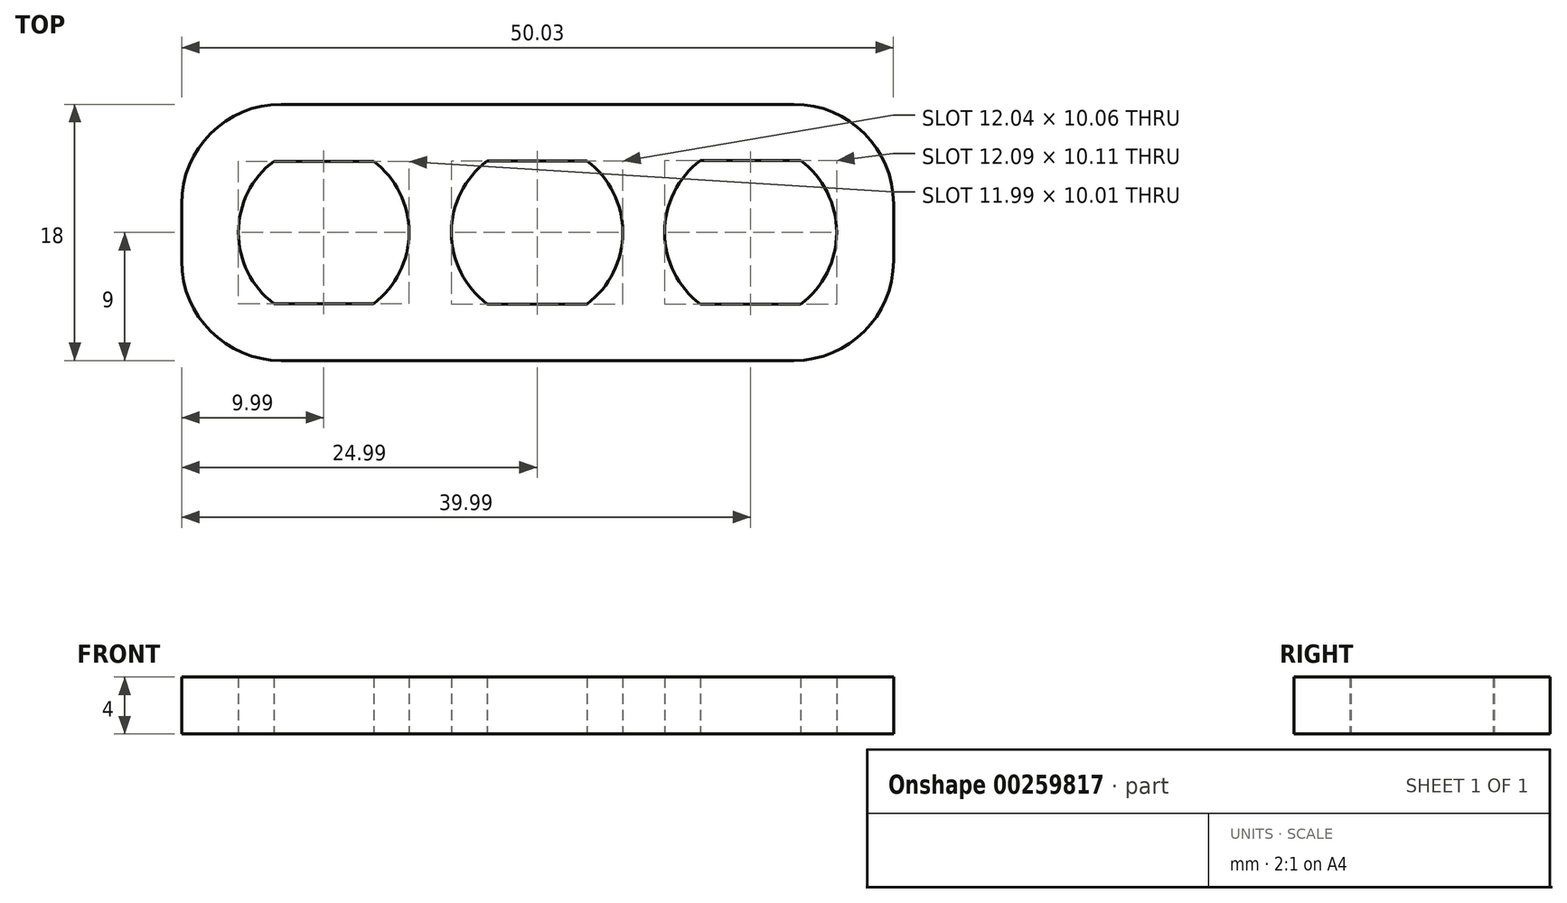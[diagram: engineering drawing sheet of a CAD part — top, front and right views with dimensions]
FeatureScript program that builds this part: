
annotation { "Feature Type Name" : "Feature", "Feature Type Description" : "" }
export const myFeature = defineFeature(function(context is Context, id is Id, definition is map)
    precondition{}
    {
        {
            var Q0;
            Q0=qCreatedBy(makeId("Top.planeOp"),FACE);
            var sketch = newSketch(context, id + "F0", { "sketchPlane" : qUnion([Q0])});
            skArc(sketch, "E0", {"start": v(-3.5, 5) * mm, "mid": v(-6, 0) * mm, "end": v(-3.5, -5) * mm, "construction": true});
            skArc(sketch, "E1", {"start": v(3.5, -5) * mm, "mid": v(6, 0) * mm, "end": v(3.5, 5) * mm, "construction": true});
            skLineSegment(sketch, "E2", {"start": v(-3.5, 5) * mm, "end": v(3.5, 5) * mm, "construction": true});
            skLineSegment(sketch, "E3", {"start": v(3.5, -5) * mm, "end": v(-3.5, -5) * mm, "construction": true});
            skPoint(sketch, "E4", {"position": v(0, 5) * mm});
            skPoint(sketch, "E5", {"position": v(-6, 0) * mm});
            skPoint(sketch, "E6", {"position": v(6, 0) * mm});
            skSolve(sketch);
        }
        {
            var Q0;
            Q0=qCreatedBy(makeId("Top.planeOp"),FACE);
            var sketch = newSketch(context, id + "F1", { "sketchPlane" : qUnion([Q0])});
            skLineSegment(sketch, "E7.0", {"start": v(-3.5, 5) * mm, "end": v(3.5, 5) * mm});
            skArc(sketch, "E8.0", {"start": v(-3.5, 5) * mm, "mid": v(-6, 0) * mm, "end": v(-3.5, -5) * mm});
            skLineSegment(sketch, "E9.0", {"start": v(3.5, -5) * mm, "end": v(-3.5, -5) * mm});
            skArc(sketch, "E10.0", {"start": v(3.5, -5) * mm, "mid": v(6, 0) * mm, "end": v(3.5, 5) * mm});
            skArc(sketch, "E11.1.0.0", {"start": v(11.5, 5) * mm, "mid": v(9, 0) * mm, "end": v(11.5, -5) * mm, "construction": true});
            skLineSegment(sketch, "E11.1.0.1", {"start": v(11.5, 5) * mm, "end": v(18.5, 5) * mm, "construction": true});
            skLineSegment(sketch, "E11.1.0.2", {"start": v(18.5, -5) * mm, "end": v(11.5, -5) * mm, "construction": true});
            skArc(sketch, "E11.1.0.3", {"start": v(18.5, -5) * mm, "mid": v(21, 0) * mm, "end": v(18.5, 5) * mm, "construction": true});
            skArc(sketch, "E11.2.0.0", {"start": v(26.5, 5) * mm, "mid": v(24, 0) * mm, "end": v(26.5, -5) * mm, "construction": true});
            skLineSegment(sketch, "E11.2.0.1", {"start": v(26.5, 5) * mm, "end": v(33.5, 5) * mm, "construction": true});
            skLineSegment(sketch, "E11.2.0.2", {"start": v(33.5, -5) * mm, "end": v(26.5, -5) * mm, "construction": true});
            skArc(sketch, "E11.2.0.3", {"start": v(33.5, -5) * mm, "mid": v(36, 0) * mm, "end": v(33.5, 5) * mm, "construction": true});
            skLineSegment(sketch, "E11.direction1", {"start": v(-3.5, -5) * mm, "end": v(11.5, -5) * mm, "construction": true});
            skArc(sketch, "E12.0", {"start": v(11.49, 5.03) * mm, "mid": v(8.98, 0) * mm, "end": v(11.49, -5.03) * mm});
            skLineSegment(sketch, "E12.1", {"start": v(11.49, 5.03) * mm, "end": v(18.51, 5.03) * mm});
            skArc(sketch, "E12.2", {"start": v(18.51, -5.03) * mm, "mid": v(21.02, 0) * mm, "end": v(18.51, 5.03) * mm});
            skLineSegment(sketch, "E12.3", {"start": v(18.51, -5.03) * mm, "end": v(11.49, -5.03) * mm});
            skArc(sketch, "E13.0", {"start": v(26.48, 5.05) * mm, "mid": v(23.96, 0) * mm, "end": v(26.48, -5.05) * mm});
            skLineSegment(sketch, "E13.1", {"start": v(26.48, 5.05) * mm, "end": v(33.52, 5.05) * mm});
            skArc(sketch, "E13.2", {"start": v(33.52, -5.05) * mm, "mid": v(36.04, 0) * mm, "end": v(33.52, 5.05) * mm});
            skLineSegment(sketch, "E13.3", {"start": v(33.52, -5.05) * mm, "end": v(26.48, -5.05) * mm});
            skLineSegment(sketch, "E14.bottom", {"start": v(-3, 9) * mm, "end": v(33.04, 9) * mm});
            skLineSegment(sketch, "E14.top", {"start": v(-3, -9) * mm, "end": v(33.04, -9) * mm});
            skLineSegment(sketch, "E14.left", {"start": v(-10, 2) * mm, "end": v(-10, -2) * mm});
            skLineSegment(sketch, "E14.right", {"start": v(40.04, 2) * mm, "end": v(40.04, -2) * mm});
            skPoint(sketch, "E15.visualSharp", {"position": v(-10, 9) * mm});
            skArc(sketch, "E15.filletArc", {"start": v(-3, 9) * mm, "mid": v(-7.94, 6.95) * mm, "end": v(-10, 2) * mm});
            skPoint(sketch, "E16.visualSharp", {"position": v(-10, -9) * mm});
            skArc(sketch, "E16.filletArc", {"start": v(-10, -2) * mm, "mid": v(-7.94, -6.95) * mm, "end": v(-3, -9) * mm});
            skPoint(sketch, "E17.visualSharp", {"position": v(40.04, -9) * mm});
            skArc(sketch, "E17.filletArc", {"start": v(33.04, -9) * mm, "mid": v(38, -6.95) * mm, "end": v(40.04, -2) * mm});
            skPoint(sketch, "E18.visualSharp", {"position": v(40.04, 9) * mm});
            skArc(sketch, "E18.filletArc", {"start": v(40.04, 2) * mm, "mid": v(38, 6.95) * mm, "end": v(33.04, 9) * mm});
            skPoint(sketch, "E19", {"position": v(-10, 0) * mm});
            skPoint(sketch, "E20", {"position": v(36.04, 0) * mm});
            skLineSegment(sketch, "E21", {"start": v(36.04, 0) * mm, "end": v(40.04, 0) * mm, "construction": true});
            skLineSegment(sketch, "E22", {"start": v(-6, 0) * mm, "end": v(-10, 0) * mm, "construction": true});
            skLineSegment(sketch, "E23", {"start": v(0, 5) * mm, "end": v(0, 9) * mm, "construction": true});
            skLineSegment(sketch, "E24", {"start": v(0, -9) * mm, "end": v(0, -5) * mm, "construction": true});
            skPoint(sketch, "E25", {"position": v(8.98, 0) * mm});
            skPoint(sketch, "E26", {"position": v(21.02, 0) * mm});
            skSolve(sketch);
        }
        {
            var Q0;
            Q0 = qSketchRegion(id + "F1", true);
            extrude(context, id + "F2", {"entities" : qUnion([Q0]), "depth" : 4 * mm});
        }
    });
